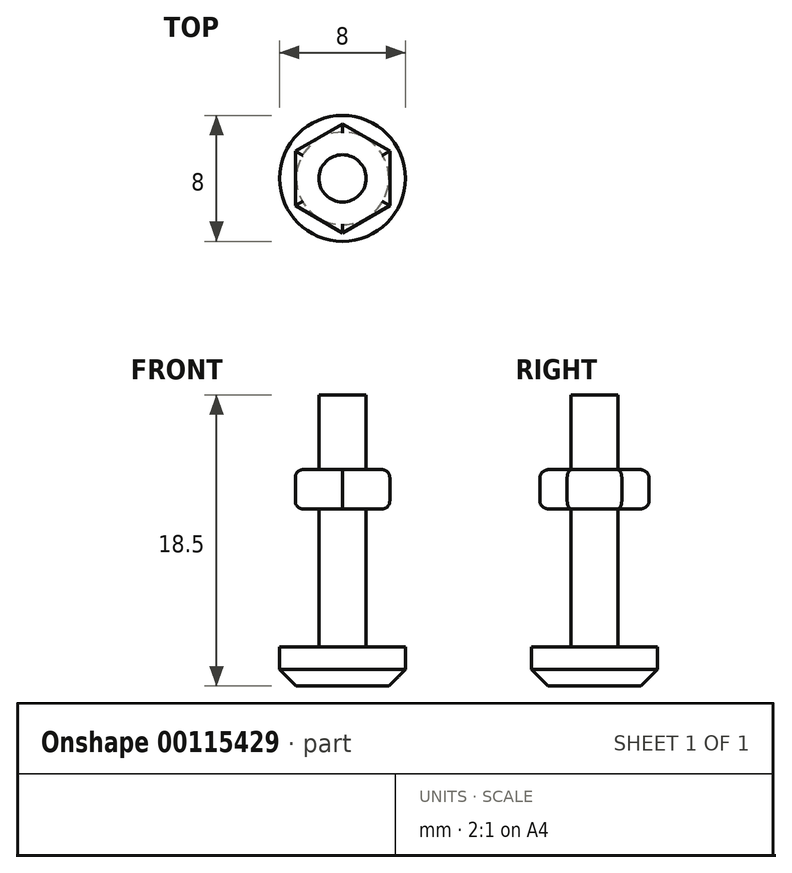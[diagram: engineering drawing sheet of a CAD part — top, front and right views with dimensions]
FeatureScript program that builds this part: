
annotation { "Feature Type Name" : "Feature", "Feature Type Description" : "" }
export const myFeature = defineFeature(function(context is Context, id is Id, definition is map)
    precondition{}
    {
        {
            var Q0;
            Q0=qCreatedBy(makeId("Front.planeOp"),FACE);
            var sketch = newSketch(context, id + "F0", { "sketchPlane" : qUnion([Q0])});
            skLineSegment(sketch, "E0", {"start": v(0, 16) * mm, "end": v(1.5, 16) * mm});
            skLineSegment(sketch, "E1", {"start": v(1.5, 16) * mm, "end": v(1.5, 0) * mm});
            skLineSegment(sketch, "E2", {"start": v(1.5, 0) * mm, "end": v(4, 0) * mm});
            skLineSegment(sketch, "E3", {"start": v(4, 0) * mm, "end": v(4, -1.44) * mm});
            skLineSegment(sketch, "E4", {"start": v(4, -1.44) * mm, "end": v(2.94, -2.5) * mm});
            skLineSegment(sketch, "E5", {"start": v(2.94, -2.5) * mm, "end": v(0, -2.5) * mm});
            skLineSegment(sketch, "E6", {"start": v(0, 16) * mm, "end": v(0, -2.5) * mm});
            skSolve(sketch);
        }
        {
            var Q0;
            Q0 = qSketchRegion(id + "F0", true);
            var Q1;
            Q1=sQuery(id+"F0.wireOp",EDGE,"E6");
            revolve(context, id + "F1", {"entities" : qUnion([Q0]), "axis" : qUnion([Q1]), "revolveType" : RevolveType.FULL});
        }
        {
            var Q0;
            Q0=makeQuery(id+"F1.opRevolve","SWEPT_FACE",FACE,{"disambiguationData":[OSD([sQuery(id+"F0.wireOp",EDGE,"E0")])]});
            cPlane(context, id + "F2", {"entities" : qUnion([Q0]), "cplaneType" : CPlaneType.OFFSET, "offset" : 6 * mm, "oppositeDirection" : true, "width" : 150 * mm, "height" : 150 * mm});
        }
        {
            var Q0;
            Q0=qCreatedBy(id+"F2.planeOp",FACE);
            var sketch = newSketch(context, id + "F3", { "sketchPlane" : qUnion([Q0])});
            skCircle(sketch, "E7.cCircle", {"center": v(0, 0) * mm, "radius": 3 * mm, "construction": true});
            skLineSegment(sketch, "E7.0", {"start": v(3, 1.73) * mm, "end": v(3, -1.73) * mm});
            skLineSegment(sketch, "E7.1", {"start": v(3, -1.73) * mm, "end": v(0, -3.46) * mm});
            skLineSegment(sketch, "E7.2", {"start": v(0, -3.46) * mm, "end": v(-3, -1.73) * mm});
            skLineSegment(sketch, "E7.3", {"start": v(-3, -1.73) * mm, "end": v(-3, 1.73) * mm});
            skLineSegment(sketch, "E7.4", {"start": v(-3, 1.73) * mm, "end": v(0, 3.46) * mm});
            skLineSegment(sketch, "E7.5", {"start": v(0, 3.46) * mm, "end": v(3, 1.73) * mm});
            skPoint(sketch, "E7.0.midPoint", {"position": v(3, 0) * mm});
            skSolve(sketch);
        }
        {
            var Q0;
            Q0 = qSketchRegion(id + "F3", true);
            extrude(context, id + "F4", {"entities" : qUnion([Q0]), "operationType" : NewBodyOperationType.ADD, "endBound" : BoundingType.SYMMETRIC, "depth" : 2.5 * mm});
        }
        {
            var Q0;
            Q0=makeQuery(id+"F4.opExtrude","CAP_EDGE",EDGE,{"disambiguationData":[OSD([sQuery(id+"F3.wireOp",EDGE,"E7.1")])],"isStart":false});
            var Q1;
            Q1=makeQuery(id+"F4.opExtrude","CAP_EDGE",EDGE,{"disambiguationData":[OSD([sQuery(id+"F3.wireOp",EDGE,"E7.0")])],"isStart":false});
            var Q2;
            Q2=makeQuery(id+"F4.opExtrude","CAP_EDGE",EDGE,{"disambiguationData":[OSD([sQuery(id+"F3.wireOp",EDGE,"E7.5")])],"isStart":false});
            var Q3;
            Q3=makeQuery(id+"F4.opExtrude","CAP_EDGE",EDGE,{"disambiguationData":[OSD([sQuery(id+"F3.wireOp",EDGE,"E7.2")])],"isStart":false});
            var Q4;
            Q4=makeQuery(id+"F4.opExtrude","CAP_EDGE",EDGE,{"disambiguationData":[OSD([sQuery(id+"F3.wireOp",EDGE,"E7.3")])],"isStart":false});
            var Q5;
            Q5=makeQuery(id+"F4.opExtrude","CAP_EDGE",EDGE,{"disambiguationData":[OSD([sQuery(id+"F3.wireOp",EDGE,"E7.4")])],"isStart":false});
            var Q6;
            Q6=makeQuery(id+"F4.opExtrude","CAP_EDGE",EDGE,{"disambiguationData":[OSD([sQuery(id+"F3.wireOp",EDGE,"E7.2")])],"isStart":true});
            var Q7;
            Q7=makeQuery(id+"F4.opExtrude","CAP_EDGE",EDGE,{"disambiguationData":[OSD([sQuery(id+"F3.wireOp",EDGE,"E7.1")])],"isStart":true});
            var Q8;
            Q8=makeQuery(id+"F4.opExtrude","CAP_EDGE",EDGE,{"disambiguationData":[OSD([sQuery(id+"F3.wireOp",EDGE,"E7.0")])],"isStart":true});
            var Q9;
            Q9=makeQuery(id+"F4.opExtrude","CAP_EDGE",EDGE,{"disambiguationData":[OSD([sQuery(id+"F3.wireOp",EDGE,"E7.3")])],"isStart":true});
            var Q10;
            Q10=makeQuery(id+"F4.opExtrude","CAP_EDGE",EDGE,{"disambiguationData":[OSD([sQuery(id+"F3.wireOp",EDGE,"E7.4")])],"isStart":true});
            var Q11;
            Q11=makeQuery(id+"F4.opExtrude","CAP_EDGE",EDGE,{"disambiguationData":[OSD([sQuery(id+"F3.wireOp",EDGE,"E7.5")])],"isStart":true});
            fillet(context, id + "F5", {"entities" : qUnion([Q0, Q1, Q2, Q3, Q4, Q5, Q6, Q7, Q8, Q9, Q10, Q11]), "radius" : 0.5 * mm, "tangentPropagation" : true, "allowEdgeOverflow" : false});
        }
    });
